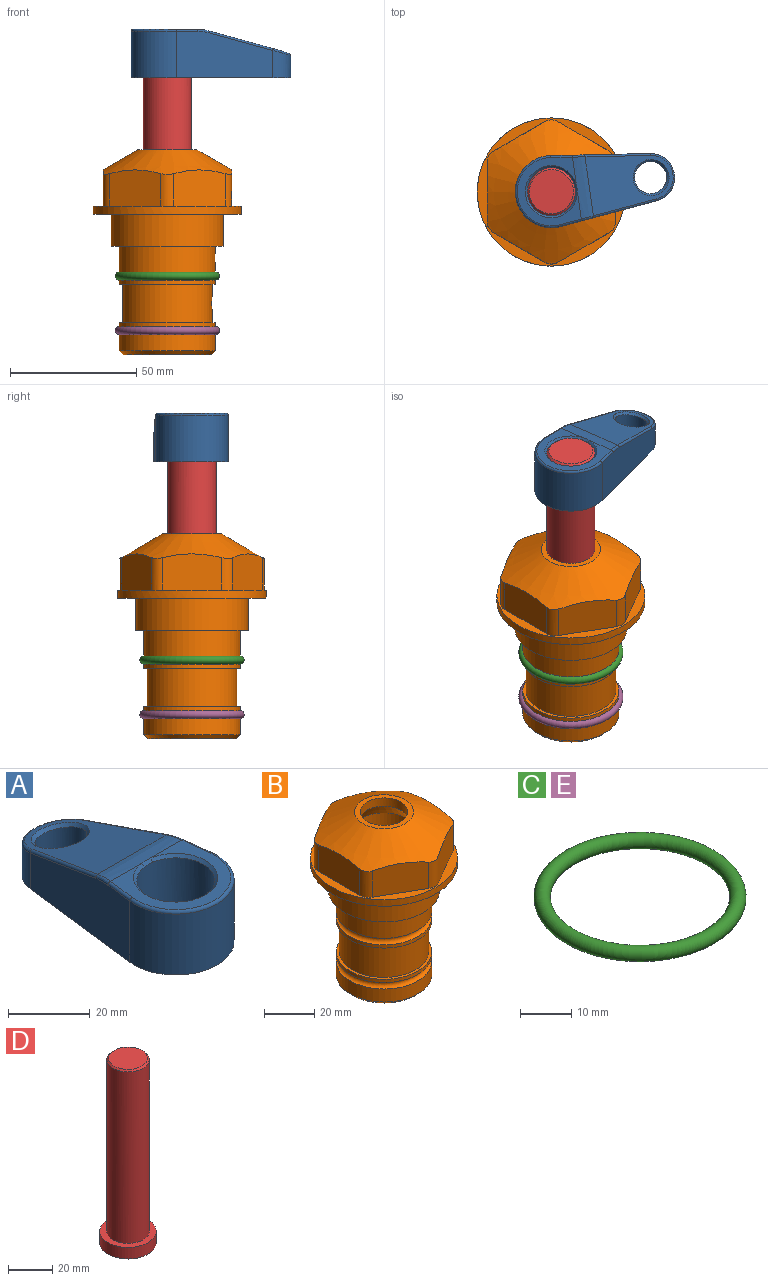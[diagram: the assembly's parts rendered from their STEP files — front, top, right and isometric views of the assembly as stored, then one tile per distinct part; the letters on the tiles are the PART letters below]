
ASSEMBLY  parts=5 mates=4
PART A: 31 faces, bbox 31.7x65.5x19.8 mm
  f0: plane 39.12x18.26mm, normal (0.99,0.12,0), area 612.2mm2, adj f1,f4,f7,f11,f13,f15
  f1: cylinder r=9.53mm len=18.91mm, axis (0,0,-1), area 296.1mm2, adj f0,f2,f7,f17
  f2: plane 39.12x18.26mm, normal (-0.99,0.12,0), area 612.2mm2, adj f1,f4,f7,f12,f14,f16
  f3: cylinder r=6.35mm len=12.7mm, axis (0,0,-1), area 362.4mm2, adj f7,f18
  f4: cylinder r=14.29mm len=28.58mm, axis (0,0,-1), area 882.2mm2, adj f0,f2,f7,f10
  f5: cylinder r=9.53mm len=19.05mm, axis (0,0,-1), area 1092.6mm2, adj f7,f19,f20
  f6: plane 26.99x23.69mm, normal (0,0,1), area 216.2mm2, adj f9,f10,f11,f12,f19
  f7: plane 63.5x28.58mm, normal (0,0,-1), area 661.8mm2, adj f0,f1,f2,f3,f4,f5,f22,f23
  f8: plane 33.52x23.6mm, normal (0,0.26,0.97), area 486mm2, adj f9,f15,f16,f17,f18
  f9: cylinder r=19.05mm len=24.72mm, axis (1,0,0), area 120.4mm2, adj f6,f8,f13,f14,f20
  f10: torus R=13.49mm, axis (0,0,1), area 59mm2, adj f4,f6,f11,f12
  f11: cylinder r=0.79mm len=8.67mm, axis (0.12,-0.99,0), area 10.8mm2, adj f0,f6,f10,f13
  f12: cylinder r=0.79mm len=8.67mm, axis (0.12,0.99,0), area 10.8mm2, adj f2,f6,f10,f14
  f13: bspline ~4.95x1.42mm, area 6.1mm2, adj f0,f9,f11,f15
  f14: bspline ~4.95x1.42mm, area 6.1mm2, adj f2,f9,f12,f16
  f15: cylinder r=0.79mm len=25.95mm, axis (0.12,-0.96,0.26), area 32.9mm2, adj f0,f8,f13,f17
  f16: cylinder r=0.79mm len=25.95mm, axis (0.12,0.96,-0.26), area 32.9mm2, adj f2,f8,f14,f17
  f17: bspline ~18.91x8.38mm, area 30mm2, adj f1,f8,f15,f16
  f18: bspline ~14.29x14.29mm, area 48.3mm2, adj f3,f8
  f19: cone r=9.53mm half-angle=45deg, axis (0,0,1), area 66.5mm2, adj f5,f6,f20
  f20: bspline ~3.22x0.96mm, area 3.5mm2, adj f5,f9,f19
  f21: plane 2.75x2.72mm, normal (0,0,-1), area 2.9mm2, adj f23,f25,f28
  f22: plane 23.05x15.88mm, normal (-0.99,-0.12,0), area 323.6mm2, adj f7,f25,f26,f27,f28,f29
  f23: plane 23.05x15.88mm, normal (0.99,-0.12,0), area 323.6mm2, adj f7,f21,f25,f27,f28,f30
  f24: cylinder r=9.53mm len=10.69mm, axis (0,0,-1), area 114.7mm2, adj f7,f27,f29,f30
  f25: cylinder r=12.7mm len=20.59mm, axis (0,0,-1), area 381.1mm2, adj f7,f21,f22,f23,f26,f28
  f26: plane 2.75x2.72mm, normal (0,0,-1), area 2.9mm2, adj f22,f25,f28
  f27: plane 19.72x18.37mm, normal (0,-0.26,-0.97), area 291.8mm2, adj f22,f23,f24,f28,f29,f30
  f28: cylinder r=15.88mm len=19.92mm, axis (1,0,0), area 54.8mm2, adj f21,f22,f23,f25,f26,f27
  f29: cylinder r=1.59mm len=11mm, axis (0,0,-1), area 34.7mm2, adj f7,f22,f24,f27
  f30: cylinder r=1.59mm len=11mm, axis (0,0,-1), area 34.7mm2, adj f7,f23,f24,f27
PART B: 36 faces, bbox 58.7x58.7x81 mm
  f0: cylinder r=17.78mm len=35.56mm, axis (0,0,1), area 1670.8mm2, adj f23,f24,f31
  f1: cylinder r=19.05mm len=38.1mm, axis (0,0,1), area 1191.9mm2, adj f26,f27,f30
  f2: plane 58.66x58.66mm, normal (0,0,-1), area 1150.6mm2, adj f3,f28
  f3: cylinder r=29.33mm len=58.66mm, axis (0,0,-1), area 585.1mm2, adj f2,f4
  f4: plane 58.66x58.66mm, normal (0,0,1), area 475.9mm2, adj f3,f5,f6,f7,f8,f9,f10,f11
  f5: plane 20.32x14.34mm, normal (-0.5,0.87,0), area 324.4mm2, adj f4,f15,f16,f17
  f6: plane 20.32x14.34mm, normal (0.5,0.87,0), area 324.4mm2, adj f4,f14,f15,f17
  f7: plane 23.48x14.34mm, normal (1,0,0), area 324.4mm2, adj f4,f13,f14,f17
  f8: plane 20.32x14.34mm, normal (0.5,-0.87,0), area 324.4mm2, adj f4,f12,f13,f17
  f9: plane 20.32x14.34mm, normal (-0.5,-0.87,0), area 324.4mm2, adj f4,f11,f12,f17
  f10: plane 23.48x14.34mm, normal (-1,0,0), area 324.4mm2, adj f4,f11,f16,f17
  f11: cylinder r=5.08mm len=12.85mm, axis (0,0,-1), area 67.2mm2, adj f4,f9,f10,f17
  f12: cylinder r=5.08mm len=12.85mm, axis (0,0,-1), area 67.2mm2, adj f4,f8,f9,f17
  f13: cylinder r=5.08mm len=12.85mm, axis (0,0,-1), area 67.2mm2, adj f4,f7,f8,f17
  f14: cylinder r=5.08mm len=12.85mm, axis (0,0,-1), area 67.2mm2, adj f4,f6,f7,f17
  f15: cylinder r=5.08mm len=12.85mm, axis (0,0,-1), area 67.2mm2, adj f4,f5,f6,f17
  f16: cylinder r=5.08mm len=12.85mm, axis (0,0,-1), area 67.2mm2, adj f4,f5,f10,f17
  f17: cone r=11.73mm half-angle=60deg, axis (0,0,-1), area 2071.8mm2, adj f5,f6,f7,f8,f9,f10,f11,f12
  f18: plane 23.46x23.46mm, normal (0,0,1), area 147.4mm2, adj f17,f35
  f19: plane 34.93x34.93mm, normal (0,0,-1), area 958mm2, adj f29
  f20: cylinder r=19.05mm len=38.1mm, axis (0,0,1), area 760.1mm2, adj f21,f29
  f21: torus R=19.05mm, axis (0,0,1), area 565.3mm2, adj f20,f22
  f22: cylinder r=19.05mm len=38.1mm, axis (0,0,1), area 190mm2, adj f21,f23
  f23: plane 38.1x38.1mm, normal (0,0,1), area 146.9mm2, adj f0,f22
  f24: plane 38.1x38.1mm, normal (0,0,-1), area 146.9mm2, adj f0,f25
  f25: cylinder r=19.05mm len=38.1mm, axis (0,0,1), area 190mm2, adj f24,f26
  f26: torus R=19.05mm, axis (0,0,1), area 565.3mm2, adj f1,f25
  f27: plane 44.45x44.45mm, normal (0,0,-1), area 411.7mm2, adj f1,f28
  f28: cylinder r=22.23mm len=44.45mm, axis (0,0,1), area 1773.5mm2, adj f2,f27
  f29: cone r=19.05mm half-angle=45deg, axis (0,0,1), area 257.5mm2, adj f19,f20
  f30: cylinder r=3.17mm len=6.75mm, axis (-1,0,0), area 128mm2, adj f1,f33
  f31: cylinder r=3.17mm len=6.35mm, axis (-1,0,0), area 102.5mm2, adj f0,f33
  f32: plane 25.4x25.4mm, normal (0,0,1), area 506.7mm2, adj f33
  f33: cylinder r=12.7mm len=66.42mm, axis (0,0,-1), area 5236.2mm2, adj f30,f31,f32,f34
  f34: cone r=9.53mm half-angle=30deg, axis (0,0,-1), area 443.4mm2, adj f33,f35
  f35: cylinder r=9.53mm len=19.05mm, axis (0,0,-1), area 240.9mm2, adj f18,f34
PART C: 1 faces, bbox 44.7x44.7x3.2 mm
  f0: torus R=19.05mm, axis (0,0,1), area 1193.9mm2
PART D: 6 faces, bbox 25.4x25.4x101.6 mm
  f0: plane 17.46x17.46mm, normal (0,0,1), area 239.5mm2, adj f5
  f1: plane 25.4x25.4mm, normal (0,0,-1), area 506.7mm2, adj f2
  f2: cylinder r=12.7mm len=25.4mm, axis (0,0,1), area 506.7mm2, adj f1,f3
  f3: plane 25.4x25.4mm, normal (0,0,1), area 221.7mm2, adj f2,f4
  f4: cylinder r=9.53mm len=94.46mm, axis (0,0,1), area 5653mm2, adj f3,f5
  f5: cone r=8.73mm half-angle=45deg, axis (0,0,-1), area 64.4mm2, adj f0,f4
PART E: same geometry as C
PLACE A rot(axis=(0,0,-1),81.9deg) t=(0,0,9.63)mm
PLACE B at identity fixed
PLACE C at identity
PLACE D rot(axis=(0,0,-1),81.9deg) t=(0,0,9.63)mm
PLACE E t=(0,0,-21.59)mm
MATE fastened A.f4 <-> D.f2  axis (0,0,1) through (0,0,73.13)mm
MATE cylindrical D.f2 <-> B.f0  axis (0,0,-1) through (0,0,-28.47)mm
MATE fastened C.f0 <-> B.f0  axis (0,0,1) through (0,0,-24.51)mm
MATE fastened E.f0 <-> B.f0  axis (0,0,1) through (0,0,-46.1)mm
